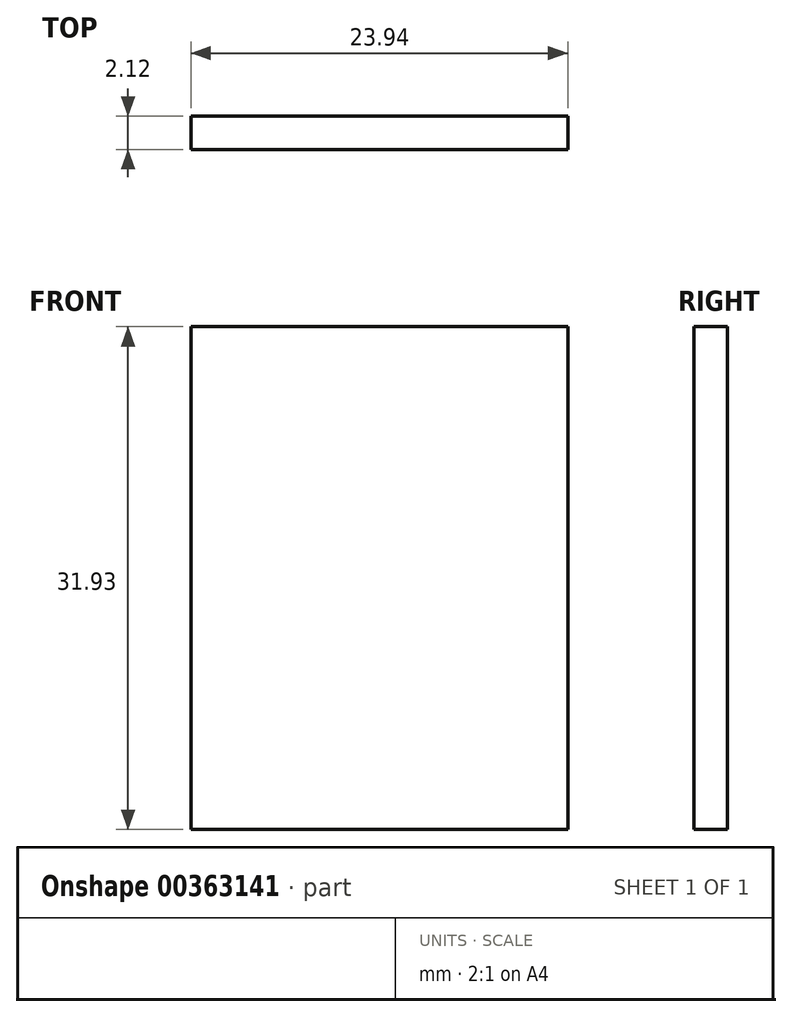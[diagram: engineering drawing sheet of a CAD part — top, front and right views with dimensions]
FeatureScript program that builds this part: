
annotation { "Feature Type Name" : "Feature", "Feature Type Description" : "" }
export const myFeature = defineFeature(function(context is Context, id is Id, definition is map)
    precondition{}
    {
        {
            var Q0;
            Q0=qCreatedBy(makeId("Front.planeOp"),FACE);
            var sketch = newSketch(context, id + "F0", { "sketchPlane" : qUnion([Q0])});
            skLineSegment(sketch, "E0.bottom", {"start": v(-10.9, 17.7) * mm, "end": v(13.05, 17.7) * mm});
            skLineSegment(sketch, "E0.top", {"start": v(-10.9, -14.23) * mm, "end": v(13.05, -14.23) * mm});
            skLineSegment(sketch, "E0.left", {"start": v(-10.9, 17.7) * mm, "end": v(-10.9, -14.23) * mm});
            skLineSegment(sketch, "E0.right", {"start": v(13.05, 17.7) * mm, "end": v(13.05, -14.23) * mm});
            skSolve(sketch);
        }
        {
            var Q0;
            Q0=makeQuery(id+"F0.imprint","IMPRINT",FACE,{"disambiguationData":[TD([[makeQuery(id+"F0.imprint","IMPRINT",EDGE,{"derivedFrom":sQuery(id+"F0.wireOp",EDGE,"E0.bottom")}),-1.0]])]});
            extrude(context, id + "F1", {"entities" : qUnion([Q0]), "depth" : 2.12 * mm});
        }
    });
